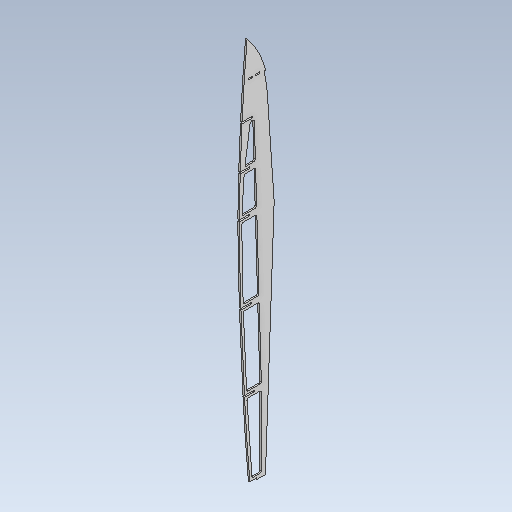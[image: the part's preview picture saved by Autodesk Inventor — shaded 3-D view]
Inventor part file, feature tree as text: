
AUTODESK INVENTOR PART (.ipt)
format: ipt  version: 2020.3 (Build 243373010, 373A)  size: 337,408 bytes
history: native  units: in
note: dims shown in document units (in); Inventor stores cm internally (conversion verified against a paired STEP export)
features: other x32, extrude x1, sketch x1
ambient origin geometry x8: Origin, YZ Plane, XZ Plane, XY Plane, X Axis, Y Axis, Z Axis, Center Point
bodies: Solid1 (feature_tree)
feature tree (34):
  other  "stringer"
  other  "base_sketch.ipt"
  extrude  "Extrusion1"  Depth=0.0787in
  other  "bulkhead_main"
  other  "bulkhead_F1"
  other  "bulkhead_front"
  other  "bulkhead_F2"
  other  "bulkhead_B1"
  other  "bulkhead_B2"
  other  "transom"
  other  "bulkhead_front_tunnel_top"
  other  "bulkhead_front_tunnel_bottom"
  other  "bulkhead_main_top"
  other  "bulkhead_main_tunnel_bottom"
  other  "bulkhead_main_tunnel_standoff"
  other  "bulkhead_front_top"
  other  "bulkhead_front_bottom"
  other  "bulkhead_F1_tunnel_bottom"
  other  "bulkhead_F1_tunnel_top"
  other  "bulkhead_F1_top"
  other  "bulkhead_F1_tunnel_standoff"
  other  "bulkhead_F1_bottom"
  other  "bulkhead_F2_bottom"
  other  "bulkhead_F2_top"
  other  "bulkhead_B1_bottom"
  other  "bulkhead_B1_top"
  other  "bulkhead_B1_tunnel_standoff"
  other  "bulkhead_B1_tunnel_bottom"
  other  "bulkhead_B2_top"
  other  "bulkhead_B2_tunnel_bottom"
  other  "bulkhead_B2_bottom"
  sketch  "Sketch9"  dims[d0=0.3937in d1=0.0787in d2=0.0787in d3=0.0787in d4=0.0in d5=0.0787in d6=0.0787in d9=0.0787in d10=0.0787in d25=0.1181in d26=0.1181in d27=0.1181in d28=0.1181in d30=0.1181in d31=0.1181in d32=0.1181in d33=0.1181in d35=0.1181in d36=0.0787in d37=0.1181in d38=0.1181in d39=0.1181in d40=0.1181in d43=0.1181in d45=0.0787in d46=0.0787in d47=0.1181in d48=0.0787in d49=0.1181in d50=0.1181in d52=0.1181in d53=0.1181in d54=0.1181in d24=0.0197in]
  other  "stringer_inside"
  other  "stinger_bottom_liner"
